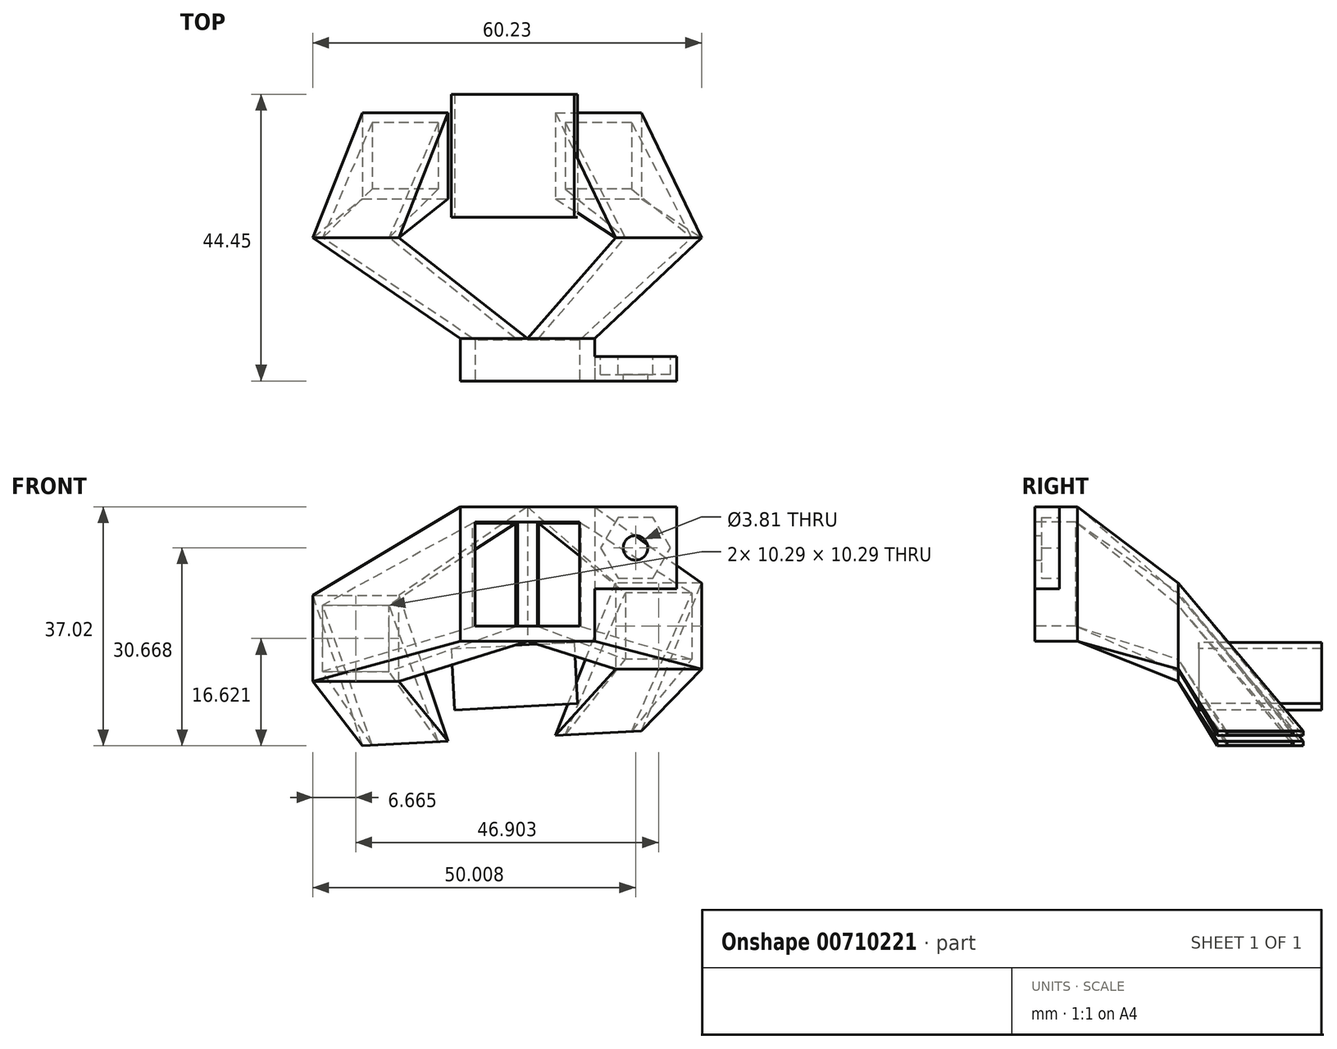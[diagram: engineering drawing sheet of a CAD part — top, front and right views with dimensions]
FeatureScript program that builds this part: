
annotation { "Feature Type Name" : "Feature", "Feature Type Description" : "" }
export const myFeature = defineFeature(function(context is Context, id is Id, definition is map)
    precondition{}
    {
        {
            var Q0;
            Q0=qCreatedBy(makeId("Front.planeOp"),FACE);
            var sketch = newSketch(context, id + "F0", { "sketchPlane" : qUnion([Q0])});
            skLineSegment(sketch, "E0.bottom", {"start": v(20.83, 20.83) * mm, "end": v(33.53, 20.83) * mm});
            skLineSegment(sketch, "E0.top", {"start": v(20.83, 8.13) * mm, "end": v(33.53, 8.13) * mm});
            skLineSegment(sketch, "E0.left", {"start": v(20.83, 20.83) * mm, "end": v(20.83, 8.13) * mm});
            skLineSegment(sketch, "E0.right", {"start": v(33.53, 20.83) * mm, "end": v(33.53, 8.13) * mm});
            skSolve(sketch);
        }
        {
            var Q0;
            Q0=makeQuery(id+"F0.imprint","IMPRINT",FACE,{"disambiguationData":[TD([[makeQuery(id+"F0.imprint","IMPRINT",EDGE,{"derivedFrom":sQuery(id+"F0.wireOp",EDGE,"E0.bottom")}),-1.0]])]});
            extrude(context, id + "F1", {"entities" : qUnion([Q0]), "oppositeDirection" : true, "depth" : 3.8 * mm, "offsetDistance" : 25.4 * mm});
        }
        {
            var Q0;
            Q0=makeQuery(id+"F1.opExtrude","CAP_FACE",FACE,{"disambiguationData":[OSD([sQuery(id+"F0.wireOp",EDGE,"E0.bottom"),sQuery(id+"F0.wireOp",EDGE,"E0.top"),sQuery(id+"F0.wireOp",EDGE,"E0.left"),sQuery(id+"F0.wireOp",EDGE,"E0.right")])],"isStart":false});
            var sketch = newSketch(context, id + "F2", { "sketchPlane" : qUnion([Q0])});
            skCircle(sketch, "E1", {"center": v(-27.18, 14.48) * mm, "radius": 1.9 * mm});
            skPoint(sketch, "E1.centerSnap0", {"position": v(-33.53, 14.48) * mm});
            skPoint(sketch, "E1.centerSnap1", {"position": v(-27.18, 20.83) * mm});
            skSolve(sketch);
        }
        {
            var Q0;
            Q0=qSketchRegion(id+"F2",true);
            extrude(context, id + "F3", {"entities" : qUnion([Q0]), "operationType" : NewBodyOperationType.REMOVE, "oppositeDirection" : true, "depth" : 25.4 * mm, "offsetDistance" : 25.4 * mm});
        }
        {
            var Q0;
            Q0=makeQuery(id+"F1.opExtrude","CAP_FACE",FACE,{"disambiguationData":[OSD([sQuery(id+"F0.wireOp",EDGE,"E0.bottom"),sQuery(id+"F0.wireOp",EDGE,"E0.top"),sQuery(id+"F0.wireOp",EDGE,"E0.left"),sQuery(id+"F0.wireOp",EDGE,"E0.right")])],"isStart":false});
            var sketch = newSketch(context, id + "F4", { "sketchPlane" : qUnion([Q0])});
            skCircle(sketch, "E2.cCircle", {"center": v(-27.18, 14.48) * mm, "radius": 4.7 * mm, "construction": true});
            skLineSegment(sketch, "E2.0", {"start": v(-24.47, 9.78) * mm, "end": v(-29.9, 9.78) * mm});
            skLineSegment(sketch, "E2.1", {"start": v(-29.9, 9.78) * mm, "end": v(-32.6, 14.48) * mm});
            skLineSegment(sketch, "E2.2", {"start": v(-32.6, 14.48) * mm, "end": v(-29.9, 19.18) * mm});
            skLineSegment(sketch, "E2.3", {"start": v(-29.9, 19.18) * mm, "end": v(-24.47, 19.18) * mm});
            skLineSegment(sketch, "E2.4", {"start": v(-24.47, 19.18) * mm, "end": v(-21.75, 14.48) * mm});
            skLineSegment(sketch, "E2.5", {"start": v(-21.75, 14.48) * mm, "end": v(-24.47, 9.78) * mm});
            skPoint(sketch, "E2.0.midPoint", {"position": v(-27.18, 9.78) * mm});
            skSolve(sketch);
        }
        {
            var Q0;
            Q0=qSketchRegion(id+"F4",true);
            extrude(context, id + "F5", {"entities" : qUnion([Q0]), "operationType" : NewBodyOperationType.REMOVE, "oppositeDirection" : true, "depth" : 2.8 * mm, "offsetDistance" : 25.4 * mm});
        }
        {
            var Q0;
            Q0=makeQuery(id+"F1.opExtrude","CAP_FACE",FACE,{"disambiguationData":[OSD([sQuery(id+"F0.wireOp",EDGE,"E0.bottom"),sQuery(id+"F0.wireOp",EDGE,"E0.top"),sQuery(id+"F0.wireOp",EDGE,"E0.left"),sQuery(id+"F0.wireOp",EDGE,"E0.right")])],"isStart":true});
            var sketch = newSketch(context, id + "F6", { "sketchPlane" : qUnion([Q0])});
            skLineSegment(sketch, "E3.bottom", {"start": v(20.83, 20.83) * mm, "end": v(0, 20.83) * mm});
            skLineSegment(sketch, "E3.top", {"start": v(20.83, 0) * mm, "end": v(0, 0) * mm});
            skLineSegment(sketch, "E3.left", {"start": v(20.83, 20.83) * mm, "end": v(20.83, 0) * mm});
            skLineSegment(sketch, "E3.right", {"start": v(0, 20.83) * mm, "end": v(0, 0) * mm});
            skSolve(sketch);
        }
        {
            var Q0;
            {var subQ3=sQuery(id+"F6.wireOp",EDGE,"E3.bottom");Q0=makeQuery(id+"F6.imprint","IMPRINT",FACE,{"disambiguationData":[TD([[makeQuery(id+"F6.imprint","IMPRINT",EDGE,{"derivedFrom":subQ3}),1.0]])]});}
            var sketch = newSketch(context, id + "F7", { "sketchPlane" : qUnion([Q0])});
            skLineSegment(sketch, "E4.bottom", {"start": v(18.5, 2.34) * mm, "end": v(2.34, 2.34) * mm});
            skLineSegment(sketch, "E4.top", {"start": v(18.5, 18.5) * mm, "end": v(2.34, 18.5) * mm});
            skLineSegment(sketch, "E4.left", {"start": v(18.5, 2.34) * mm, "end": v(18.5, 18.5) * mm});
            skLineSegment(sketch, "E4.right", {"start": v(2.34, 2.34) * mm, "end": v(2.34, 18.5) * mm});
            skPoint(sketch, "E4.middle", {"position": v(10.41, 10.41) * mm});
            skSolve(sketch);
        }
        {
            var Q0;
            Q0=makeQuery(id+"F7.imprint","IMPRINT",FACE,{"disambiguationData":[TD([[makeQuery(id+"F7.imprint","IMPRINT",EDGE,{"derivedFrom":sQuery(id+"F7.wireOp",EDGE,"E4.bottom")}),1.0]])]});
            extrude(context, id + "F8", {"entities" : qUnion([Q0]), "operationType" : NewBodyOperationType.ADD, "oppositeDirection" : true, "depth" : 6.35 * mm, "offsetDistance" : 25.4 * mm});
        }
        {
            var Q0;
            Q0=makeQuery(id+"F8.opExtrude","CAP_FACE",FACE,{"disambiguationData":[OSD([sQuery(id+"F6.wireOp",EDGE,"E3.bottom"),sQuery(id+"F6.wireOp",EDGE,"E3.top"),sQuery(id+"F6.wireOp",EDGE,"E3.left"),sQuery(id+"F6.wireOp",EDGE,"E3.right"),sQuery(id+"F7.wireOp",EDGE,"E4.bottom"),sQuery(id+"F7.wireOp",EDGE,"E4.top"),sQuery(id+"F7.wireOp",EDGE,"E4.left"),sQuery(id+"F7.wireOp",EDGE,"E4.right")])],"isStart":false});
            cPlane(context, id + "F9", {"entities" : qUnion([Q0]), "cplaneType" : CPlaneType.OFFSET, "offset" : 28.57 * mm, "width" : 152.4 * mm, "height" : 152.4 * mm});
        }
        {
            var Q0;
            Q0=qCreatedBy(id+"F9.planeOp",FACE);
            var sketch = newSketch(context, id + "F10", { "sketchPlane" : qUnion([Q0])});
            skLineSegment(sketch, "E5", {"start": v(-20.84, 0) * mm, "end": v(-21.83, -19.02) * mm, "construction": true});
            skLineSegment(sketch, "E6", {"start": v(-20.84, 0) * mm, "end": v(-20.84, -19.05) * mm, "construction": true});
            skLineSegment(sketch, "E7", {"start": v(-21.83, -19.02) * mm, "end": v(-5.98, -19.85) * mm, "construction": true});
            skLineSegment(sketch, "E8", {"start": v(-5.98, -19.85) * mm, "end": v(-4.98, -0.83) * mm, "construction": true});
            skSolve(sketch);
        }
        {
            var Q0;
            Q0=sQuery(id+"F10.wireOp",EDGE,"E8");
            cPlane(context, id + "F11", {"entities" : qUnion([Q0]), "cplaneType" : CPlaneType.MID_PLANE, "offset" : 25.4 * mm, "width" : 152.4 * mm, "height" : 152.4 * mm});
        }
        {
            var Q0;
            Q0=qCreatedBy(id+"F11.planeOp",FACE);
            var sketch = newSketch(context, id + "F12", { "sketchPlane" : qUnion([Q0])});
            skLineSegment(sketch, "E9.bottom", {"start": v(-1.42, 44.45) * mm, "end": v(17.63, 44.45) * mm});
            skLineSegment(sketch, "E9.top", {"start": v(-1.42, 25.4) * mm, "end": v(17.63, 25.4) * mm});
            skLineSegment(sketch, "E9.left", {"start": v(-1.42, 44.45) * mm, "end": v(-1.42, 25.4) * mm});
            skLineSegment(sketch, "E9.right", {"start": v(17.63, 44.45) * mm, "end": v(17.63, 25.4) * mm});
            skPoint(sketch, "E9.middle", {"position": v(8.1, 34.93) * mm});
            skSolve(sketch);
        }
        {
            var Q0;
            Q0=qSketchRegion(id+"F12",true);
            extrude(context, id + "F13", {"entities" : qUnion([Q0]), "depth" : 9.52 * mm, "offsetDistance" : 25.4 * mm});
        }
        {
            var Q0;
            Q0=qCreatedBy(id+"F11.planeOp",FACE);
            cPlane(context, id + "F14", {"entities" : qUnion([Q0]), "cplaneType" : CPlaneType.OFFSET, "offset" : 4.76 * mm, "oppositeDirection" : true, "width" : 152.4 * mm, "height" : 152.4 * mm});
        }
        {
            var Q0;
            Q0=qCreatedBy(id+"F14.planeOp",FACE);
            var sketch = newSketch(context, id + "F15", { "sketchPlane" : qUnion([Q0])});
            skLineSegment(sketch, "E10", {"start": v(28.15, 34.93) * mm, "end": v(-17.98, 34.93) * mm, "construction": true});
            skSolve(sketch);
        }
        {
            var Q0;
            Q0=qCreatedBy(id+"F14.planeOp",FACE);
            var sketch = newSketch(context, id + "F16", { "sketchPlane" : qUnion([Q0])});
            skLineSegment(sketch, "E11.bottom", {"start": v(25.8, 40.07) * mm, "end": v(15.52, 40.07) * mm});
            skLineSegment(sketch, "E11.top", {"start": v(25.8, 29.78) * mm, "end": v(15.52, 29.78) * mm});
            skLineSegment(sketch, "E11.left", {"start": v(25.8, 40.07) * mm, "end": v(25.8, 29.78) * mm});
            skLineSegment(sketch, "E11.right", {"start": v(15.52, 40.07) * mm, "end": v(15.52, 29.78) * mm});
            skPoint(sketch, "E11.middle", {"position": v(20.66, 34.93) * mm});
            skLineSegment(sketch, "E12.bottom", {"start": v(-4.18, 40.07) * mm, "end": v(-14.47, 40.07) * mm});
            skLineSegment(sketch, "E12.top", {"start": v(-4.18, 29.78) * mm, "end": v(-14.47, 29.78) * mm});
            skLineSegment(sketch, "E12.left", {"start": v(-4.18, 40.07) * mm, "end": v(-4.18, 29.78) * mm});
            skLineSegment(sketch, "E12.right", {"start": v(-14.47, 40.07) * mm, "end": v(-14.47, 29.78) * mm});
            skPoint(sketch, "E12.middle", {"position": v(-9.33, 34.93) * mm});
            skSolve(sketch);
        }
        {
            var Q0;
            Q0=qCreatedBy(id+"F14.planeOp",FACE);
            var sketch = newSketch(context, id + "F17", { "sketchPlane" : qUnion([Q0])});
            skLineSegment(sketch, "E13.bottom", {"start": v(14, 41.6) * mm, "end": v(27.33, 41.6) * mm});
            skLineSegment(sketch, "E13.top", {"start": v(14, 28.26) * mm, "end": v(27.33, 28.26) * mm});
            skLineSegment(sketch, "E13.left", {"start": v(14, 41.6) * mm, "end": v(14, 28.26) * mm});
            skLineSegment(sketch, "E13.right", {"start": v(27.33, 41.6) * mm, "end": v(27.33, 28.26) * mm});
            skPoint(sketch, "E13.middle", {"position": v(20.66, 34.93) * mm});
            skLineSegment(sketch, "E14.bottom", {"start": v(-16, 41.6) * mm, "end": v(-2.66, 41.6) * mm});
            skLineSegment(sketch, "E14.top", {"start": v(-16, 28.26) * mm, "end": v(-2.66, 28.26) * mm});
            skLineSegment(sketch, "E14.left", {"start": v(-16, 41.6) * mm, "end": v(-16, 28.26) * mm});
            skLineSegment(sketch, "E14.right", {"start": v(-2.66, 41.6) * mm, "end": v(-2.66, 28.26) * mm});
            skPoint(sketch, "E14.middle", {"position": v(-9.33, 34.93) * mm});
            skSolve(sketch);
        }
        {
            var Q0;
            Q0=makeQuery(id+"F13.opExtrude","SWEPT_FACE",FACE,{"disambiguationData":[OSD([sQuery(id+"F12.wireOp",EDGE,"E9.top")])]});
            cPlane(context, id + "F18", {"entities" : qUnion([Q0]), "cplaneType" : CPlaneType.OFFSET, "offset" : 3.17 * mm, "width" : 152.4 * mm, "height" : 152.4 * mm});
        }
        {
            var Q0;
            Q0=qCreatedBy(id+"F18.planeOp",FACE);
            var sketch = newSketch(context, id + "F19", { "sketchPlane" : qUnion([Q0])});
            skLineSegment(sketch, "E15.bottom", {"start": v(35.88, 7.48) * mm, "end": v(25.6, 7.48) * mm});
            skLineSegment(sketch, "E15.top", {"start": v(35.88, -2.8) * mm, "end": v(25.6, -2.8) * mm});
            skLineSegment(sketch, "E15.left", {"start": v(35.88, 7.48) * mm, "end": v(35.88, -2.8) * mm});
            skLineSegment(sketch, "E15.right", {"start": v(25.6, 7.48) * mm, "end": v(25.6, -2.8) * mm});
            skPoint(sketch, "E15.middle", {"position": v(30.74, 2.34) * mm});
            skSolve(sketch);
        }
        {
            var Q0;
            Q0=qCreatedBy(id+"F18.planeOp",FACE);
            var sketch = newSketch(context, id + "F20", { "sketchPlane" : qUnion([Q0])});
            skLineSegment(sketch, "E16.bottom", {"start": v(37.4, 9) * mm, "end": v(24.07, 9) * mm});
            skLineSegment(sketch, "E16.top", {"start": v(37.4, -4.33) * mm, "end": v(24.07, -4.33) * mm});
            skLineSegment(sketch, "E16.left", {"start": v(37.4, 9) * mm, "end": v(37.4, -4.33) * mm});
            skLineSegment(sketch, "E16.right", {"start": v(24.07, 9) * mm, "end": v(24.07, -4.33) * mm});
            skPoint(sketch, "E16.middle", {"position": v(30.74, 2.34) * mm});
            skSolve(sketch);
        }
        {
            var Q0;
            Q0=makeQuery(id+"F17.imprint","IMPRINT",FACE,{"disambiguationData":[TD([[makeQuery(id+"F17.imprint","IMPRINT",EDGE,{"derivedFrom":sQuery(id+"F17.wireOp",EDGE,"E13.bottom")}),-1.0]])]});
            var Q1;
            Q1=makeQuery(id+"F20.imprint","IMPRINT",FACE,{"disambiguationData":[TD([[makeQuery(id+"F20.imprint","IMPRINT",EDGE,{"derivedFrom":sQuery(id+"F20.wireOp",EDGE,"E16.bottom")}),1.0]])]});
            loft(context, id + "F21", {"sheetProfilesArray" : [{ "sheetProfileEntities" : qUnion([Q0]) }, { "sheetProfileEntities" : qUnion([Q1]) }]});
        }
        {
            var Q1;
            Q1=makeQuery(id+"F16.imprint","IMPRINT",FACE,{"disambiguationData":[TD([[makeQuery(id+"F16.imprint","IMPRINT",EDGE,{"derivedFrom":sQuery(id+"F16.wireOp",EDGE,"E11.bottom")}),1.0]])]});
            var Q2;
            Q2 = qSketchRegion(id + "F19", true);
            loft(context, id + "F22", {"operationType" : NewBodyOperationType.REMOVE, "sheetProfilesArray" : [{ "sheetProfileEntities" : qUnion([Q1]) }, { "sheetProfileEntities" : qUnion([Q2]) }]});
        }
        {
            var Q0;
            Q0=qCreatedBy(id+"F18.planeOp",FACE);
            var sketch = newSketch(context, id + "F23", { "sketchPlane" : qUnion([Q0])});
            skLineSegment(sketch, "E17.bottom", {"start": v(-21.3, -4.71) * mm, "end": v(-11.02, -4.71) * mm});
            skLineSegment(sketch, "E17.top", {"start": v(-21.3, 5.57) * mm, "end": v(-11.02, 5.57) * mm});
            skLineSegment(sketch, "E17.left", {"start": v(-21.3, -4.71) * mm, "end": v(-21.3, 5.57) * mm});
            skLineSegment(sketch, "E17.right", {"start": v(-11.02, -4.71) * mm, "end": v(-11.02, 5.57) * mm});
            skPoint(sketch, "E17.middle", {"position": v(-16.17, 0.43) * mm});
            skSolve(sketch);
        }
        {
            var Q0;
            Q0=qCreatedBy(id+"F18.planeOp",FACE);
            var sketch = newSketch(context, id + "F24", { "sketchPlane" : qUnion([Q0])});
            skLineSegment(sketch, "E18.bottom", {"start": v(-22.83, -6.24) * mm, "end": v(-9.5, -6.24) * mm});
            skLineSegment(sketch, "E18.top", {"start": v(-22.83, 7.1) * mm, "end": v(-9.5, 7.1) * mm});
            skLineSegment(sketch, "E18.left", {"start": v(-22.83, -6.24) * mm, "end": v(-22.83, 7.1) * mm});
            skLineSegment(sketch, "E18.right", {"start": v(-9.5, -6.24) * mm, "end": v(-9.5, 7.1) * mm});
            skPoint(sketch, "E18.middle", {"position": v(-16.17, 0.43) * mm});
            skSolve(sketch);
        }
        {
            var Q0;
            Q0=makeQuery(id+"F24.imprint","IMPRINT",FACE,{"disambiguationData":[TD([[makeQuery(id+"F24.imprint","IMPRINT",EDGE,{"derivedFrom":sQuery(id+"F24.wireOp",EDGE,"E18.bottom")}),1.0]])]});
            var Q1;
            Q1=makeQuery(id+"F17.imprint","IMPRINT",FACE,{"disambiguationData":[TD([[makeQuery(id+"F17.imprint","IMPRINT",EDGE,{"derivedFrom":sQuery(id+"F17.wireOp",EDGE,"E14.bottom")}),-1.0]])]});
            loft(context, id + "F25", {"sheetProfilesArray" : [{ "sheetProfileEntities" : qUnion([Q0]) }, { "sheetProfileEntities" : qUnion([Q1]) }]});
        }
        {
            var Q1;
            Q1=makeQuery(id+"F16.imprint","IMPRINT",FACE,{"disambiguationData":[TD([[makeQuery(id+"F16.imprint","IMPRINT",EDGE,{"derivedFrom":sQuery(id+"F16.wireOp",EDGE,"E12.bottom")}),1.0]])]});
            var Q2;
            Q2 = qSketchRegion(id + "F23", true);
            loft(context, id + "F26", {"operationType" : NewBodyOperationType.REMOVE, "sheetProfilesArray" : [{ "sheetProfileEntities" : qUnion([Q1]) }, { "sheetProfileEntities" : qUnion([Q2]) }]});
        }
        {
            var Q0;
            Q0=makeQuery(id+"F8.opExtrude","CAP_FACE",FACE,{"disambiguationData":[OSD([sQuery(id+"F6.wireOp",EDGE,"E3.bottom"),sQuery(id+"F6.wireOp",EDGE,"E3.top"),sQuery(id+"F6.wireOp",EDGE,"E3.left"),sQuery(id+"F6.wireOp",EDGE,"E3.right"),sQuery(id+"F7.wireOp",EDGE,"E4.bottom"),sQuery(id+"F7.wireOp",EDGE,"E4.top"),sQuery(id+"F7.wireOp",EDGE,"E4.left"),sQuery(id+"F7.wireOp",EDGE,"E4.right")])],"isStart":false});
            var sketch = newSketch(context, id + "F27", { "sketchPlane" : qUnion([Q0])});
            skLineSegment(sketch, "E19.bottom", {"start": v(-20.83, 20.83) * mm, "end": v(-10.41, 20.83) * mm});
            skLineSegment(sketch, "E19.top", {"start": v(-20.83, 0) * mm, "end": v(-10.41, 0) * mm});
            skLineSegment(sketch, "E19.left", {"start": v(-20.83, 20.83) * mm, "end": v(-20.83, 0) * mm});
            skLineSegment(sketch, "E19.right", {"start": v(-10.41, 20.83) * mm, "end": v(-10.41, 0) * mm});
            skSolve(sketch);
        }
        {
            var Q0;
            {var subQ0=makeQuery(id+"F8.opExtrude","CAP_EDGE",EDGE,{"disambiguationData":[OSD([sQuery(id+"F7.wireOp",EDGE,"E4.right")])],"isStart":false});Q0=makeQuery(id+"F27.imprint","IMPRINT",FACE,{"disambiguationData":[TD([[makeQuery(id+"F27.imprint","IMPRINT",EDGE,{"derivedFrom":subQ0}),-1.0]])]});}
            var sketch = newSketch(context, id + "F28", { "sketchPlane" : qUnion([Q0])});
            skLineSegment(sketch, "E20.bottom", {"start": v(0, 0) * mm, "end": v(-10.41, 0) * mm});
            skLineSegment(sketch, "E20.top", {"start": v(0, 20.83) * mm, "end": v(-10.41, 20.83) * mm});
            skLineSegment(sketch, "E20.left", {"start": v(0, 0) * mm, "end": v(0, 20.83) * mm});
            skLineSegment(sketch, "E20.right", {"start": v(-10.41, 0) * mm, "end": v(-10.41, 20.83) * mm});
            skSolve(sketch);
        }
        {
            var Q0;
            {var subQ1=sQuery(id+"F27.wireOp",EDGE,"E19.bottom");Q0=makeQuery(id+"F27.imprint","IMPRINT",FACE,{"disambiguationData":[TD([[makeQuery(id+"F27.imprint","IMPRINT",EDGE,{"derivedFrom":subQ1}),-1.0]])]});}
            var sketch = newSketch(context, id + "F29", { "sketchPlane" : qUnion([Q0])});
            skLineSegment(sketch, "E21.bottom", {"start": v(-18.5, 2.34) * mm, "end": v(-11.94, 2.34) * mm});
            skLineSegment(sketch, "E21.top", {"start": v(-18.5, 18.5) * mm, "end": v(-11.94, 18.5) * mm});
            skLineSegment(sketch, "E21.left", {"start": v(-18.5, 2.34) * mm, "end": v(-18.5, 18.5) * mm});
            skLineSegment(sketch, "E21.right", {"start": v(-11.94, 2.34) * mm, "end": v(-11.94, 18.5) * mm});
            skSolve(sketch);
        }
        {
            var Q0;
            {var subQ6=sQuery(id+"F28.wireOp",EDGE,"E20.bottom");Q0=makeQuery(id+"F28.imprint","IMPRINT",FACE,{"disambiguationData":[TD([[makeQuery(id+"F28.imprint","IMPRINT",EDGE,{"derivedFrom":subQ6}),1.0]])]});}
            var sketch = newSketch(context, id + "F30", { "sketchPlane" : qUnion([Q0])});
            skLineSegment(sketch, "E22.bottom", {"start": v(-8.89, 18.5) * mm, "end": v(-2.34, 18.5) * mm});
            skLineSegment(sketch, "E22.top", {"start": v(-8.89, 2.34) * mm, "end": v(-2.34, 2.34) * mm});
            skLineSegment(sketch, "E22.left", {"start": v(-8.89, 18.5) * mm, "end": v(-8.89, 2.34) * mm});
            skLineSegment(sketch, "E22.right", {"start": v(-2.34, 18.5) * mm, "end": v(-2.34, 2.34) * mm});
            skSolve(sketch);
        }
        {
            var Q0;
            Q0 = qSketchRegion(id + "F27", true);
            extrude(context, id + "F31", {"entities" : qUnion([Q0]), "operationType" : NewBodyOperationType.ADD, "depth" : 0.25 * mm, "offsetDistance" : 25.4 * mm});
        }
        {
            var Q0;
            Q0 = qSketchRegion(id + "F28", true);
            extrude(context, id + "F32", {"entities" : qUnion([Q0]), "operationType" : NewBodyOperationType.ADD, "depth" : 0.25 * mm, "offsetDistance" : 25.4 * mm});
        }
        {
            var Q0;
            Q0=makeQuery(id+"F32.boolean.opBoolean","MERGE",FACE,{"derivedFrom":[makeQuery(id+"F31.opExtrude","CAP_FACE",FACE,{"disambiguationData":[OSD([sQuery(id+"F27.wireOp",EDGE,"E19.bottom"),sQuery(id+"F27.wireOp",EDGE,"E19.top"),sQuery(id+"F27.wireOp",EDGE,"E19.left"),sQuery(id+"F27.wireOp",EDGE,"E19.right")])],"isStart":false}),makeQuery(id+"F32.opExtrude","CAP_FACE",FACE,{"disambiguationData":[OSD([sQuery(id+"F28.wireOp",EDGE,"E20.bottom"),sQuery(id+"F28.wireOp",EDGE,"E20.top"),sQuery(id+"F28.wireOp",EDGE,"E20.left"),sQuery(id+"F28.wireOp",EDGE,"E20.right")])],"isStart":false})]});
            var sketch = newSketch(context, id + "F33", { "sketchPlane" : qUnion([Q0])});
            skLineSegment(sketch, "E23", {"start": v(-10.41, 20.83) * mm, "end": v(-10.41, 0) * mm});
            skSolve(sketch);
        }
        {
            var Q0;
            {var subQ0=sQuery(id+"F33.wireOp",EDGE,"E23");Q0=makeQuery(id+"F33.imprint","IMPRINT",FACE,{"disambiguationData":[TD([[makeQuery(id+"F33.imprint","IMPRINT",EDGE,{"derivedFrom":subQ0}),-1.0]])]});}
            var Q1;
            Q1 = qSketchRegion(id + "F20", true);
            loft(context, id + "F34", {"sheetProfilesArray" : [{ "sheetProfileEntities" : qUnion([Q0]) }, { "sheetProfileEntities" : qUnion([Q1]) }]});
        }
        {
            var Q0;
            Q0 = qSketchRegion(id + "F29", true);
            extrude(context, id + "F35", {"entities" : qUnion([Q0]), "operationType" : NewBodyOperationType.REMOVE, "depth" : 0.25 * mm, "offsetDistance" : 25.4 * mm});
        }
        {
            var Q1;
            Q1 = qSketchRegion(id + "F29", true);
            var Q2;
            Q2 = qSketchRegion(id + "F19", true);
            loft(context, id + "F36", {"operationType" : NewBodyOperationType.REMOVE, "sheetProfilesArray" : [{ "sheetProfileEntities" : qUnion([Q1]) }, { "sheetProfileEntities" : qUnion([Q2]) }]});
        }
        {
            var Q0;
            Q0=makeQuery(id+"F32.boolean.opBoolean","MERGE",FACE,{"derivedFrom":[makeQuery(id+"F31.opExtrude","CAP_FACE",FACE,{"disambiguationData":[OSD([sQuery(id+"F27.wireOp",EDGE,"E19.bottom"),sQuery(id+"F27.wireOp",EDGE,"E19.top"),sQuery(id+"F27.wireOp",EDGE,"E19.left"),sQuery(id+"F27.wireOp",EDGE,"E19.right")])],"isStart":false}),makeQuery(id+"F32.opExtrude","CAP_FACE",FACE,{"disambiguationData":[OSD([sQuery(id+"F28.wireOp",EDGE,"E20.bottom"),sQuery(id+"F28.wireOp",EDGE,"E20.top"),sQuery(id+"F28.wireOp",EDGE,"E20.left"),sQuery(id+"F28.wireOp",EDGE,"E20.right")])],"isStart":false})]});
            var sketch = newSketch(context, id + "F37", { "sketchPlane" : qUnion([Q0])});
            skLineSegment(sketch, "E24.bottom", {"start": v(-10.41, 20.83) * mm, "end": v(0, 20.83) * mm});
            skLineSegment(sketch, "E24.top", {"start": v(-10.41, 0) * mm, "end": v(0, 0) * mm});
            skLineSegment(sketch, "E24.left", {"start": v(-10.41, 20.83) * mm, "end": v(-10.41, 0) * mm});
            skLineSegment(sketch, "E24.right", {"start": v(0, 20.83) * mm, "end": v(0, 0) * mm});
            skSolve(sketch);
        }
        {
            var Q0;
            Q0 = qSketchRegion(id + "F37", true);
            var Q1;
            Q1 = qSketchRegion(id + "F24", true);
            loft(context, id + "F38", {"sheetProfilesArray" : [{ "sheetProfileEntities" : qUnion([Q0]) }, { "sheetProfileEntities" : qUnion([Q1]) }]});
        }
        {
            var Q0;
            Q0 = qSketchRegion(id + "F30", true);
            extrude(context, id + "F39", {"entities" : qUnion([Q0]), "operationType" : NewBodyOperationType.REMOVE, "depth" : 0.25 * mm, "offsetDistance" : 25.4 * mm});
        }
        {
            var Q1;
            Q1 = qSketchRegion(id + "F30", true);
            var Q2;
            Q2 = qSketchRegion(id + "F23", true);
            loft(context, id + "F40", {"operationType" : NewBodyOperationType.REMOVE, "sheetProfilesArray" : [{ "sheetProfileEntities" : qUnion([Q1]) }, { "sheetProfileEntities" : qUnion([Q2]) }]});
        }
    });
